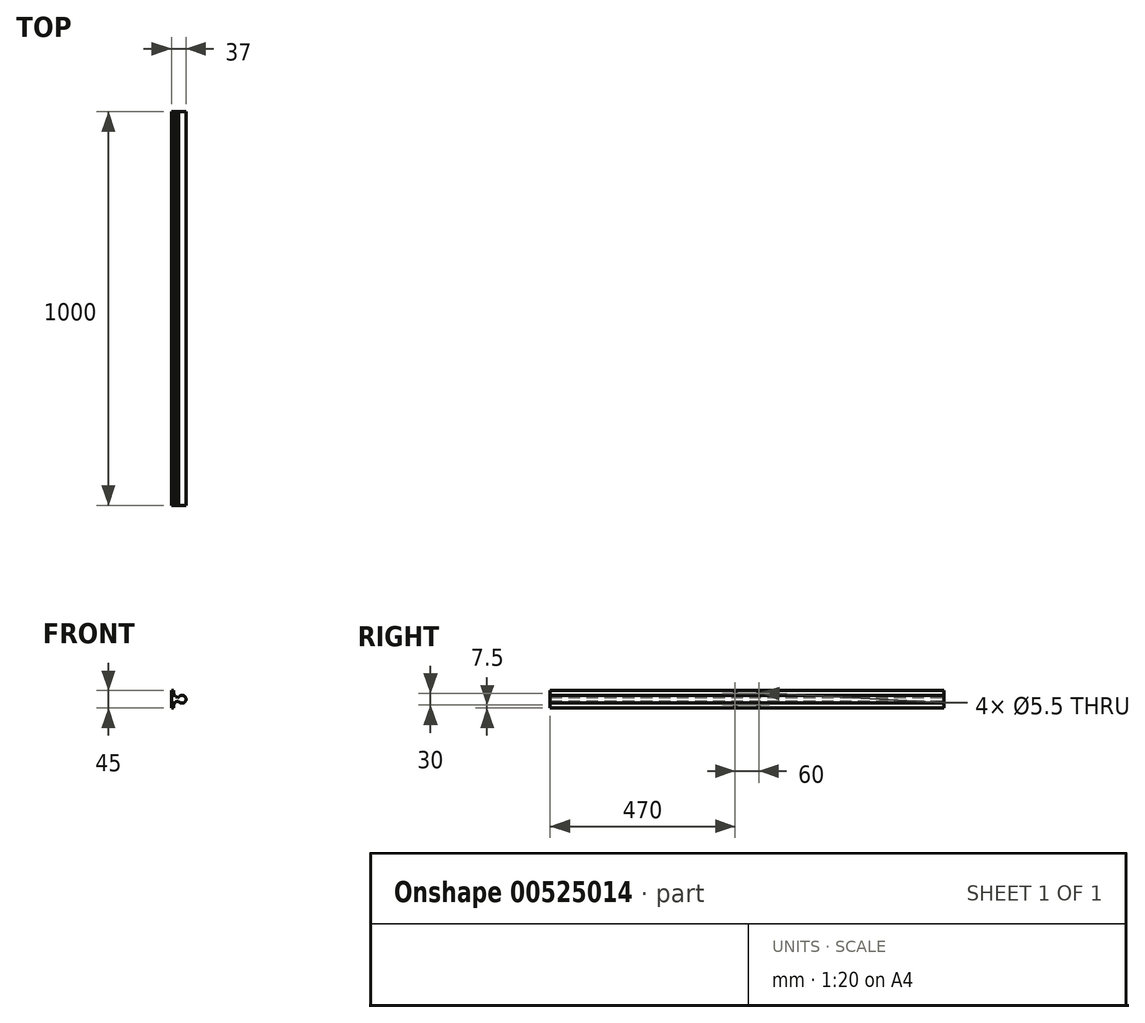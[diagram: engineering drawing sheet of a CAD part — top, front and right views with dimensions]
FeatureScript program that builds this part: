
annotation { "Feature Type Name" : "Feature", "Feature Type Description" : "" }
export const myFeature = defineFeature(function(context is Context, id is Id, definition is map)
    precondition{}
    {
        {
            var Q0;
            Q0=qCreatedBy(makeId("Front.planeOp"),FACE);
            var sketch = newSketch(context, id + "F0", { "sketchPlane" : qUnion([Q0])});
            skLineSegment(sketch, "E0.bottom", {"start": v(0, 22.5) * mm, "end": v(5, 22.5) * mm});
            skLineSegment(sketch, "E0.top", {"start": v(0, -22.5) * mm, "end": v(5, -22.5) * mm});
            skLineSegment(sketch, "E0.left", {"start": v(0, 22.5) * mm, "end": v(0, -22.5) * mm});
            skLineSegment(sketch, "E0.right", {"start": v(5, 22.5) * mm, "end": v(5, 9.5) * mm});
            skLineSegment(sketch, "E1.bottom", {"start": v(5, 9.5) * mm, "end": v(10, 9.5) * mm});
            skLineSegment(sketch, "E1.top", {"start": v(5, -9.5) * mm, "end": v(10, -9.5) * mm});
            skLineSegment(sketch, "E1.right", {"start": v(10, 9.5) * mm, "end": v(10, 6.38) * mm});
            skLineSegment(sketch, "E2", {"start": v(10, 6.38) * mm, "end": v(17.89, 4.12) * mm});
            skLineSegment(sketch, "E3", {"start": v(17.92, -4.2) * mm, "end": v(10, -6.5) * mm});
            skArc(sketch, "E4", {"start": v(17.92, -4.2) * mm, "mid": v(37, 0.04) * mm, "end": v(17.89, 4.12) * mm});
            skLineSegment(sketch, "E5.trimOffspring", {"start": v(5, -9.5) * mm, "end": v(5, -22.5) * mm});
            skLineSegment(sketch, "E6.trimOffspring", {"start": v(10, -6.5) * mm, "end": v(10, -9.5) * mm});
            skPoint(sketch, "E7.orphan", {"position": v(32.3, 0) * mm});
            skSolve(sketch);
        }
        {
            var Q0;
            Q0 = qSketchRegion(id + "F0", true);
            extrude(context, id + "F1", {"entities" : qUnion([Q0]), "endBound" : BoundingType.SYMMETRIC, "depth" : 1000 * mm, "offsetDistance" : 25 * mm});
        }
        {
            var Q0;
            Q0=makeQuery(id+"F1.opExtrude","SWEPT_FACE",FACE,{"disambiguationData":[OSD([sQuery(id+"F0.wireOp",EDGE,"E0.left")])]});
            var sketch = newSketch(context, id + "F2", { "sketchPlane" : qUnion([Q0])});
            skCircle(sketch, "E8", {"center": v(30, 15) * mm, "radius": 2.75 * mm});
            skCircle(sketch, "E9", {"center": v(30, -15) * mm, "radius": 2.75 * mm});
            skCircle(sketch, "E10", {"center": v(-30, -15) * mm, "radius": 2.75 * mm});
            skCircle(sketch, "E11", {"center": v(-30, 15) * mm, "radius": 2.75 * mm});
            skSolve(sketch);
        }
        {
            var Q0;
            Q0 = qSketchRegion(id + "F2", true);
            extrude(context, id + "F3", {"entities" : qUnion([Q0]), "operationType" : NewBodyOperationType.REMOVE, "oppositeDirection" : true, "depth" : 5 * mm, "offsetDistance" : 25 * mm});
        }
    });
